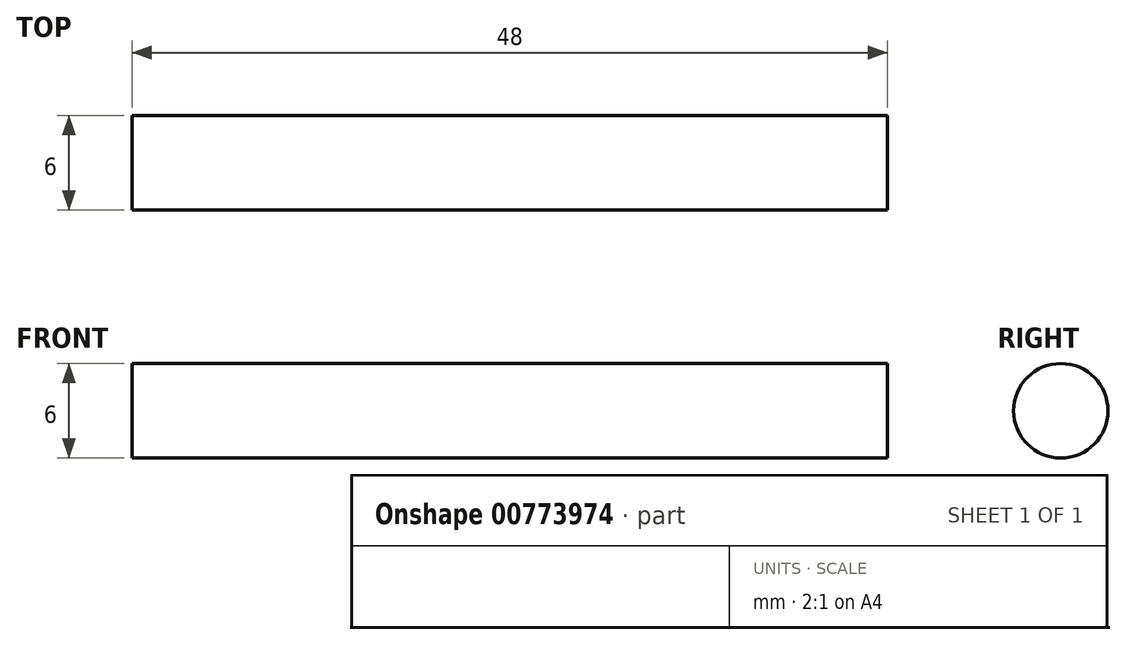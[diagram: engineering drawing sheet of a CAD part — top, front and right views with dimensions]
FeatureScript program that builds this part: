
annotation { "Feature Type Name" : "Feature", "Feature Type Description" : "" }
export const myFeature = defineFeature(function(context is Context, id is Id, definition is map)
    precondition{}
    {
        {
            var Q0;
            Q0=qCreatedBy(makeId("Right.planeOp"),FACE);
            var sketch = newSketch(context, id + "F0", { "sketchPlane" : qUnion([Q0])});
            skCircle(sketch, "E0", {"center": v(0, 0) * mm, "radius": 3 * mm});
            skSolve(sketch);
        }
        {
            var Q0;
            Q0 = qSketchRegion(id + "F0", true);
            extrude(context, id + "F1", {"entities" : qUnion([Q0]), "depth" : 48 * mm, "offsetDistance" : 25 * mm});
        }
    });
